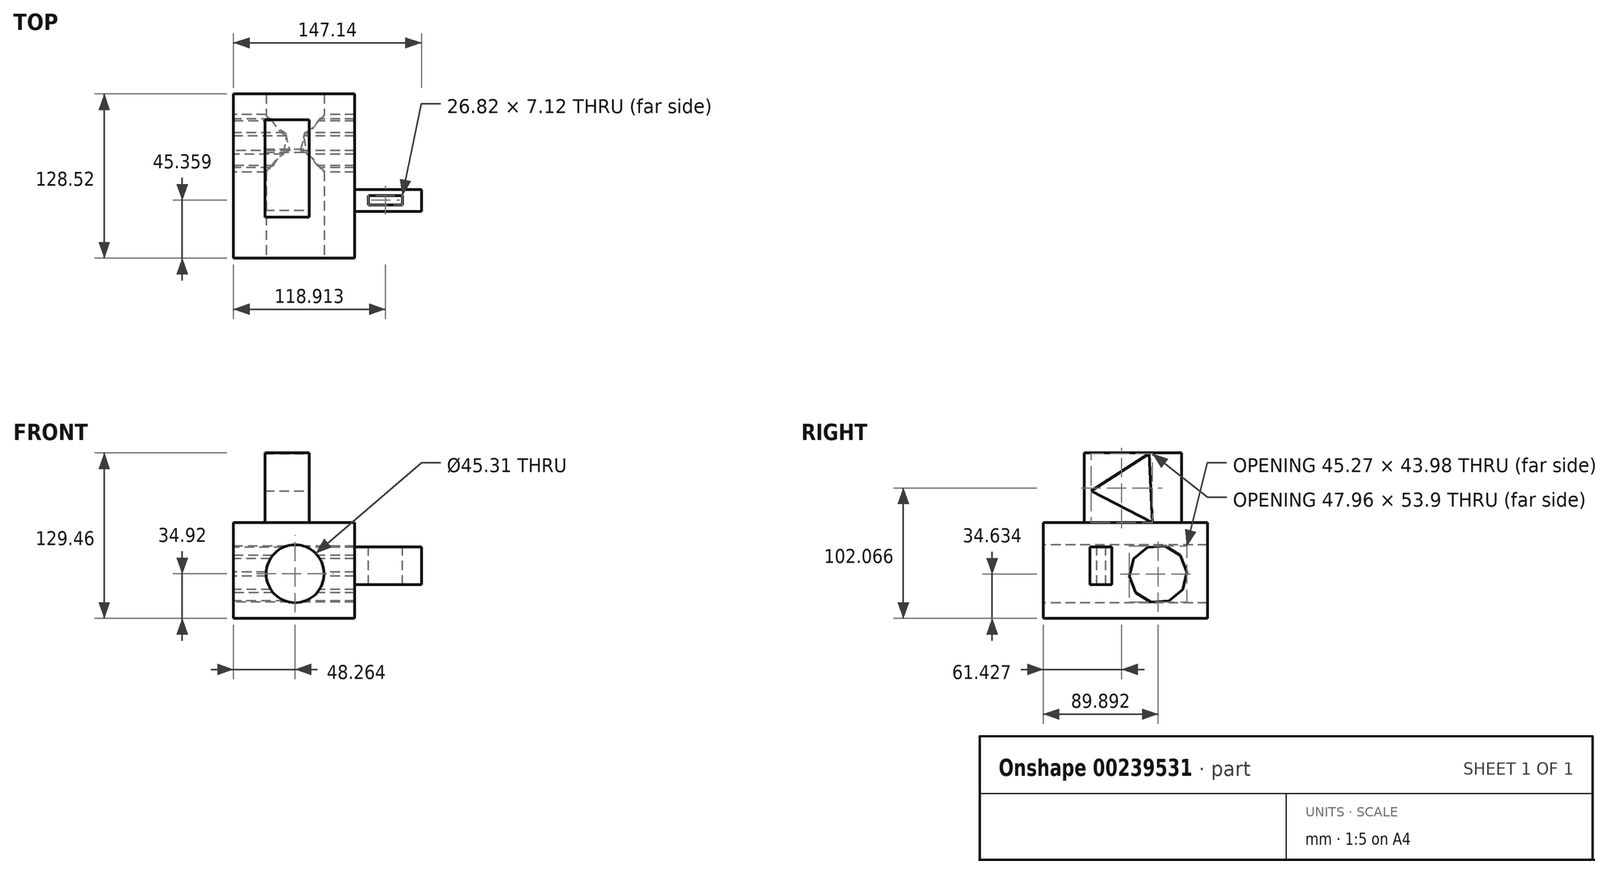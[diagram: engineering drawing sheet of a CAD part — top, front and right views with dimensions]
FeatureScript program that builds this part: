
annotation { "Feature Type Name" : "Feature", "Feature Type Description" : "" }
export const myFeature = defineFeature(function(context is Context, id is Id, definition is map)
    precondition{}
    {
        {
            var Q0;
            Q0=qCreatedBy(makeId("Front.planeOp"),FACE);
            var sketch = newSketch(context, id + "F0", { "sketchPlane" : qUnion([Q0])});
            skLineSegment(sketch, "E0.bottom", {"start": v(-35.63, 37.8) * mm, "end": v(59.13, 37.8) * mm});
            skLineSegment(sketch, "E0.top", {"start": v(-35.63, -37.26) * mm, "end": v(59.13, -37.26) * mm});
            skLineSegment(sketch, "E0.left", {"start": v(-35.63, 37.8) * mm, "end": v(-35.63, -37.26) * mm});
            skLineSegment(sketch, "E0.right", {"start": v(59.13, 37.8) * mm, "end": v(59.13, -37.26) * mm});
            skSolve(sketch);
        }
        {
            var Q0;
            Q0 = qSketchRegion(id + "F0", true);
            extrude(context, id + "F1", {"entities" : qUnion([Q0]), "endBound" : BoundingType.SYMMETRIC, "depth" : 128.52 * mm});
        }
        {
            var Q0;
            Q0=qCreatedBy(makeId("Top.planeOp"),FACE);
            var sketch = newSketch(context, id + "F2", { "sketchPlane" : qUnion([Q0])});
            skLineSegment(sketch, "E1.bottom", {"start": v(23.76, -32.13) * mm, "end": v(-11.07, -32.13) * mm});
            skLineSegment(sketch, "E1.top", {"start": v(23.76, 44.01) * mm, "end": v(-11.07, 44.01) * mm});
            skLineSegment(sketch, "E1.left", {"start": v(23.76, -32.13) * mm, "end": v(23.76, 44.01) * mm});
            skLineSegment(sketch, "E1.right", {"start": v(-11.07, -32.13) * mm, "end": v(-11.07, 44.01) * mm});
            skSolve(sketch);
        }
        {
            var Q0;
            Q0 = qSketchRegion(id + "F2", true);
            extrude(context, id + "F3", {"entities" : qUnion([Q0]), "operationType" : NewBodyOperationType.ADD, "depth" : 92.2 * mm});
        }
        {
            var Q0;
            Q0=qCreatedBy(makeId("Right.planeOp"),FACE);
            var sketch = newSketch(context, id + "F4", { "sketchPlane" : qUnion([Q0])});
            skLineSegment(sketch, "E2.bottom", {"start": v(-27.6, 18.61) * mm, "end": v(-10.51, 18.61) * mm});
            skLineSegment(sketch, "E2.top", {"start": v(-27.6, -10.95) * mm, "end": v(-10.51, -10.95) * mm});
            skLineSegment(sketch, "E2.left", {"start": v(-27.6, 18.61) * mm, "end": v(-27.6, -10.95) * mm});
            skLineSegment(sketch, "E2.right", {"start": v(-10.51, 18.61) * mm, "end": v(-10.51, -10.95) * mm});
            skSolve(sketch);
        }
        {
            var Q0;
            Q0 = qSketchRegion(id + "F4", true);
            extrude(context, id + "F5", {"entities" : qUnion([Q0]), "operationType" : NewBodyOperationType.ADD, "depth" : 111.5 * mm});
        }
        {
            var Q0;
            Q0=makeQuery(id+"F5.opExtrude","SWEPT_FACE",FACE,{"disambiguationData":[OSD([sQuery(id+"F4.wireOp",EDGE,"E2.bottom")])]});
            var sketch = newSketch(context, id + "F6", { "sketchPlane" : qUnion([Q0])});
            skLineSegment(sketch, "E3.bottom", {"start": v(96.7, -22.46) * mm, "end": v(69.87, -22.46) * mm});
            skLineSegment(sketch, "E3.top", {"start": v(96.7, -15.34) * mm, "end": v(69.87, -15.34) * mm});
            skLineSegment(sketch, "E3.left", {"start": v(96.7, -22.46) * mm, "end": v(96.7, -15.34) * mm});
            skLineSegment(sketch, "E3.right", {"start": v(69.87, -22.46) * mm, "end": v(69.87, -15.34) * mm});
            skSolve(sketch);
        }
        {
            var Q0;
            Q0 = qSketchRegion(id + "F6", true);
            extrude(context, id + "F7", {"entities" : qUnion([Q0]), "operationType" : NewBodyOperationType.REMOVE, "oppositeDirection" : true, "depth" : 117.37 * mm});
        }
        {
            var Q0;
            Q0=qCreatedBy(makeId("Front.planeOp"),FACE);
            var sketch = newSketch(context, id + "F8", { "sketchPlane" : qUnion([Q0])});
            skCircle(sketch, "E4", {"center": v(12.63, -2.34) * mm, "radius": 22.66 * mm});
            skSolve(sketch);
        }
        {
            var Q0;
            Q0 = qSketchRegion(id + "F8", true);
            extrude(context, id + "F9", {"entities" : qUnion([Q0]), "operationType" : NewBodyOperationType.REMOVE, "endBound" : BoundingType.SYMMETRIC, "oppositeDirection" : true, "depth" : 229.1 * mm});
        }
        {
            var Q0;
            Q0=makeQuery(id+"F3.opExtrude","SWEPT_FACE",FACE,{"disambiguationData":[OSD([sQuery(id+"F2.wireOp",EDGE,"E1.left")])]});
            var sketch = newSketch(context, id + "F10", { "sketchPlane" : qUnion([Q0])});
            skCircle(sketch, "E5.cCircle", {"center": v(4.3, 64.06) * mm, "radius": 15.58 * mm, "construction": true});
            skLineSegment(sketch, "E5.0", {"start": v(-26.81, 62.58) * mm, "end": v(18.57, 91.75) * mm});
            skLineSegment(sketch, "E5.1", {"start": v(18.57, 91.75) * mm, "end": v(21.15, 37.86) * mm});
            skLineSegment(sketch, "E5.2", {"start": v(21.15, 37.86) * mm, "end": v(-26.81, 62.58) * mm});
            skPoint(sketch, "E5.0.midPoint", {"position": v(-4.12, 77.16) * mm});
            skSolve(sketch);
        }
        {
            var Q0;
            Q0 = qSketchRegion(id + "F10", true);
            extrude(context, id + "F11", {"entities" : qUnion([Q0]), "operationType" : NewBodyOperationType.REMOVE, "endBound" : BoundingType.SYMMETRIC, "oppositeDirection" : true, "depth" : 146.8 * mm});
        }
        {
            var Q0;
            Q0=makeQuery(id+"F1.opExtrude","SWEPT_FACE",FACE,{"disambiguationData":[OSD([sQuery(id+"F0.wireOp",EDGE,"E0.left")])]});
            var sketch = newSketch(context, id + "F12", { "sketchPlane" : qUnion([Q0])});
            skCircle(sketch, "E6.cCircle", {"center": v(-25.63, -2.63) * mm, "radius": 22.68 * mm, "construction": true});
            skLineSegment(sketch, "E6.0", {"start": v(-6.44, 9.47) * mm, "end": v(-3, -4.12) * mm});
            skLineSegment(sketch, "E6.1", {"start": v(-3, -4.12) * mm, "end": v(-8.2, -17.14) * mm});
            skLineSegment(sketch, "E6.2", {"start": v(-8.2, -17.14) * mm, "end": v(-20.06, -24.61) * mm});
            skLineSegment(sketch, "E6.3", {"start": v(-20.06, -24.61) * mm, "end": v(-34.05, -23.69) * mm});
            skLineSegment(sketch, "E6.4", {"start": v(-34.05, -23.69) * mm, "end": v(-44.82, -14.72) * mm});
            skLineSegment(sketch, "E6.5", {"start": v(-44.82, -14.72) * mm, "end": v(-48.27, -1.13) * mm});
            skLineSegment(sketch, "E6.6", {"start": v(-48.27, -1.13) * mm, "end": v(-43.06, 11.89) * mm});
            skLineSegment(sketch, "E6.7", {"start": v(-43.06, 11.89) * mm, "end": v(-31.2, 19.36) * mm});
            skLineSegment(sketch, "E6.8", {"start": v(-31.2, 19.36) * mm, "end": v(-17.21, 18.44) * mm});
            skLineSegment(sketch, "E6.9", {"start": v(-17.21, 18.44) * mm, "end": v(-6.44, 9.47) * mm});
            skSolve(sketch);
        }
        {
            var Q0;
            Q0 = qSketchRegion(id + "F12", true);
            extrude(context, id + "F13", {"entities" : qUnion([Q0]), "operationType" : NewBodyOperationType.REMOVE, "oppositeDirection" : true, "depth" : 151.38 * mm});
        }
    });
